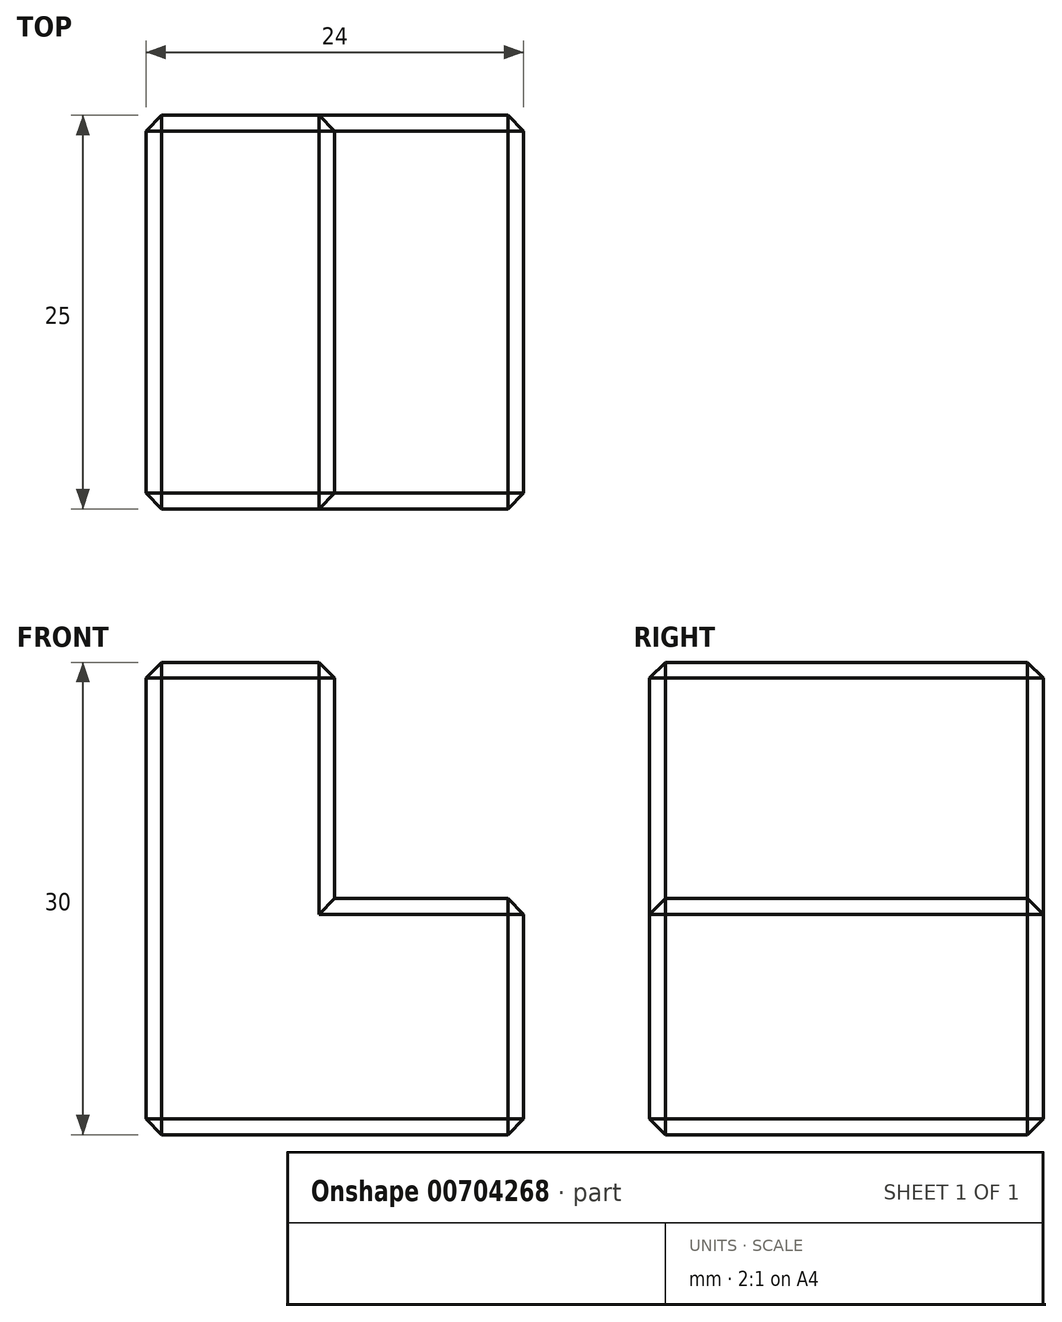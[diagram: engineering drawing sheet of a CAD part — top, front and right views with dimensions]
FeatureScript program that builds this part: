
annotation { "Feature Type Name" : "Feature", "Feature Type Description" : "" }
export const myFeature = defineFeature(function(context is Context, id is Id, definition is map)
    precondition{}
    {
        {
            var Q0;
            Q0=qCreatedBy(makeId("Front.planeOp"),FACE);
            var sketch = newSketch(context, id + "F0", { "sketchPlane" : qUnion([Q0])});
            skLineSegment(sketch, "E0", {"start": v(-12, 15) * mm, "end": v(-12, 0) * mm});
            skLineSegment(sketch, "E1", {"start": v(-12, 15) * mm, "end": v(0, 15) * mm});
            skLineSegment(sketch, "E2", {"start": v(0, 15) * mm, "end": v(0, 0) * mm});
            skLineSegment(sketch, "E3", {"start": v(0, 0) * mm, "end": v(12, 0) * mm});
            skLineSegment(sketch, "E4", {"start": v(12, 0) * mm, "end": v(12, -15) * mm});
            skLineSegment(sketch, "E5", {"start": v(12, -15) * mm, "end": v(-12, -15) * mm});
            skLineSegment(sketch, "E6", {"start": v(-12, -15) * mm, "end": v(-12, 0) * mm});
            skSolve(sketch);
        }
        {
            var Q0;
            Q0 = qSketchRegion(id + "F0", true);
            extrude(context, id + "F1", {"entities" : qUnion([Q0]), "depth" : 25 * mm, "offsetDistance" : 25 * mm});
        }
        {
            var Q0;
            Q0=makeQuery(id+"F1.opExtrude","CAP_FACE",FACE,{"disambiguationData":[OSD([sQuery(id+"F0.wireOp",EDGE,"E0"),sQuery(id+"F0.wireOp",EDGE,"E1"),sQuery(id+"F0.wireOp",EDGE,"E2"),sQuery(id+"F0.wireOp",EDGE,"E3"),sQuery(id+"F0.wireOp",EDGE,"E4"),sQuery(id+"F0.wireOp",EDGE,"E5"),sQuery(id+"F0.wireOp",EDGE,"E6")])],"isStart":false});
            var Q1;
            Q1=makeQuery(id+"F1.opExtrude","SWEPT_FACE",FACE,{"disambiguationData":[OSD([sQuery(id+"F0.wireOp",EDGE,"E1")])]});
            var Q2;
            Q2=makeQuery(id+"F1.opExtrude","CAP_FACE",FACE,{"disambiguationData":[OSD([sQuery(id+"F0.wireOp",EDGE,"E0"),sQuery(id+"F0.wireOp",EDGE,"E1"),sQuery(id+"F0.wireOp",EDGE,"E2"),sQuery(id+"F0.wireOp",EDGE,"E3"),sQuery(id+"F0.wireOp",EDGE,"E4"),sQuery(id+"F0.wireOp",EDGE,"E5"),sQuery(id+"F0.wireOp",EDGE,"E6")])],"isStart":true});
            var Q3;
            Q3=makeQuery(id+"F1.opExtrude","SWEPT_FACE",FACE,{"disambiguationData":[OSD([sQuery(id+"F0.wireOp",EDGE,"E5")])]});
            var Q4;
            Q4=makeQuery(id+"F1.opExtrude","SWEPT_FACE",FACE,{"disambiguationData":[OSD([sQuery(id+"F0.wireOp",EDGE,"E4")])]});
            var Q5;
            Q5=makeQuery(id+"F1.opExtrude","SWEPT_FACE",FACE,{"disambiguationData":[OSD([sQuery(id+"F0.wireOp",EDGE,"E0"),sQuery(id+"F0.wireOp",EDGE,"E6")])]});
            chamfer(context, id + "F2", {"entities" : qUnion([Q0, Q1, Q2, Q3, Q4, Q5]), "width" : 1 * mm, "tangentPropagation" : true});
        }
    });
